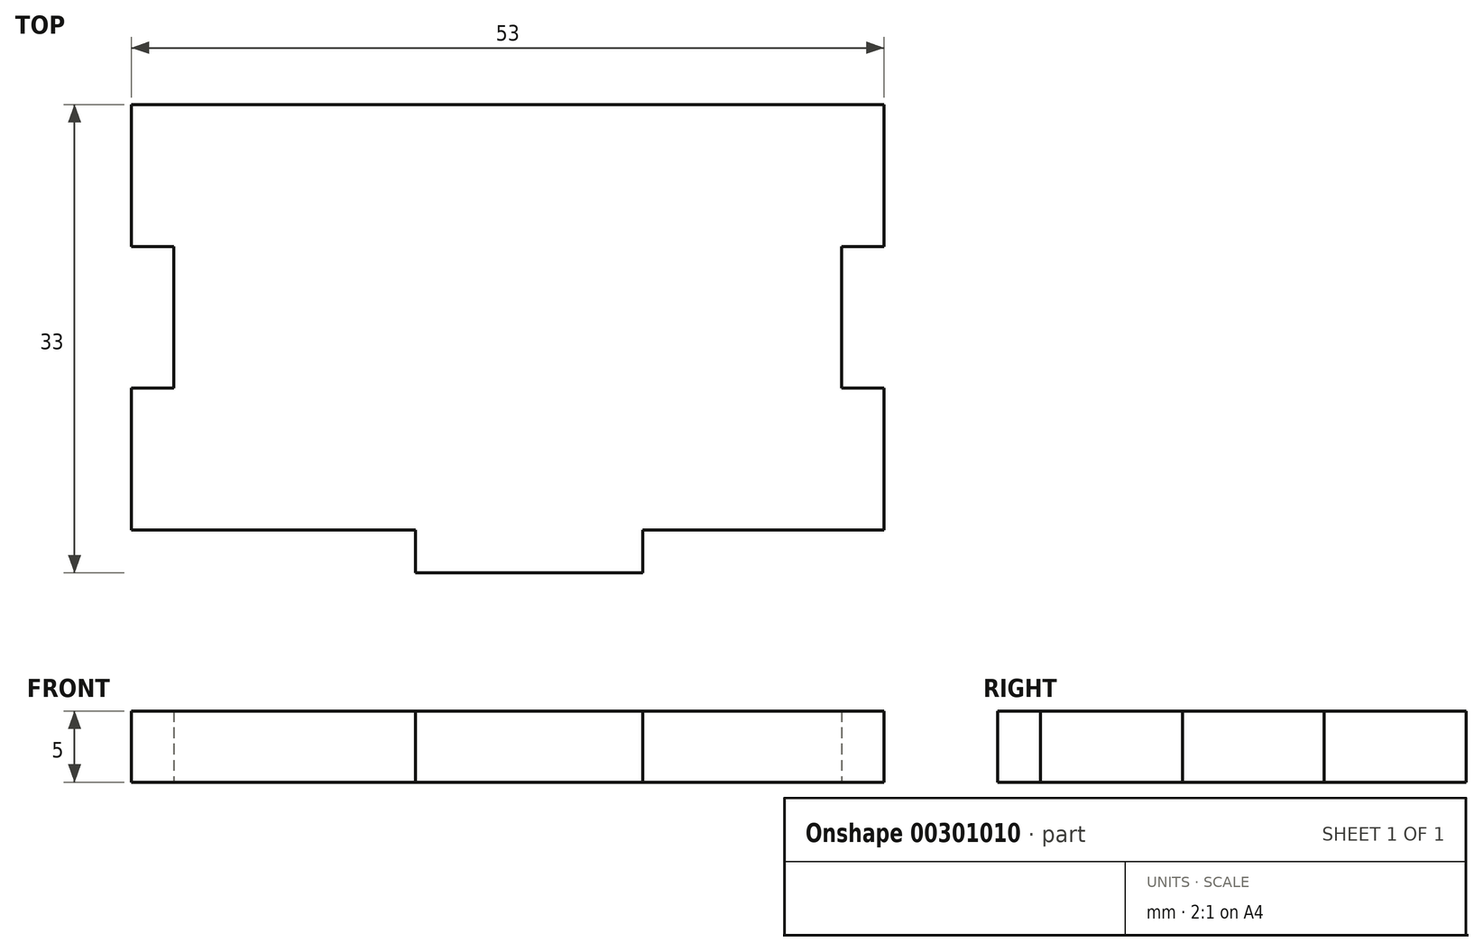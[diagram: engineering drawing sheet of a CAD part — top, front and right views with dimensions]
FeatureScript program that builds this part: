
annotation { "Feature Type Name" : "Feature", "Feature Type Description" : "" }
export const myFeature = defineFeature(function(context is Context, id is Id, definition is map)
    precondition{}
    {
        {
            var Q0;
            Q0=qCreatedBy(makeId("Top.planeOp"),FACE);
            var sketch = newSketch(context, id + "F0", { "sketchPlane" : qUnion([Q0])});
            skLineSegment(sketch, "E0.bottom", {"start": v(-26.5, 16.5) * mm, "end": v(26.5, 16.5) * mm});
            skLineSegment(sketch, "E1", {"start": v(-23.5, -13.5) * mm, "end": v(-6.5, -13.5) * mm});
            skLineSegment(sketch, "E2", {"start": v(26.5, -13.5) * mm, "end": v(9.5, -13.5) * mm});
            skLineSegment(sketch, "E3", {"start": v(-6.5, -13.5) * mm, "end": v(-6.5, -16.5) * mm});
            skLineSegment(sketch, "E4", {"start": v(-6.5, -16.5) * mm, "end": v(9.5, -16.5) * mm});
            skLineSegment(sketch, "E5", {"start": v(9.5, -16.5) * mm, "end": v(9.5, -13.5) * mm});
            skLineSegment(sketch, "E6", {"start": v(26.5, 16.5) * mm, "end": v(26.5, 6.5) * mm});
            skLineSegment(sketch, "E7", {"start": v(26.5, -13.5) * mm, "end": v(26.5, -3.5) * mm});
            skLineSegment(sketch, "E8", {"start": v(26.5, 6.5) * mm, "end": v(23.5, 6.5) * mm});
            skLineSegment(sketch, "E9", {"start": v(26.5, -3.5) * mm, "end": v(23.5, -3.5) * mm});
            skLineSegment(sketch, "E10", {"start": v(23.5, 6.5) * mm, "end": v(23.5, -3.5) * mm});
            skLineSegment(sketch, "E11.MirrorCS", {"start": v(-26.5, -3.5) * mm, "end": v(-23.5, -3.5) * mm});
            skLineSegment(sketch, "E12.MirrorCS", {"start": v(-26.5, 6.5) * mm, "end": v(-23.5, 6.5) * mm});
            skLineSegment(sketch, "E13.MirrorCS", {"start": v(-23.5, 6.5) * mm, "end": v(-23.5, -3.5) * mm});
            skLineSegment(sketch, "E14.MirrorCS", {"start": v(-26.5, -13.5) * mm, "end": v(-26.5, -3.5) * mm});
            skLineSegment(sketch, "E15.MirrorCS", {"start": v(-26.5, -13.5) * mm, "end": v(-9.5, -13.5) * mm});
            skLineSegment(sketch, "E16.MirrorCS", {"start": v(-26.5, 16.5) * mm, "end": v(-26.5, 6.5) * mm});
            skSolve(sketch);
        }
        {
            var Q0;
            Q0=makeQuery(id+"F0.imprint","IMPRINT",FACE,{"disambiguationData":[TD([[makeQuery(id+"F0.imprint","IMPRINT",EDGE,{"derivedFrom":sQuery(id+"F0.wireOp",EDGE,"E0.bottom")}),-1.0]])]});
            extrude(context, id + "F1", {"entities" : qUnion([Q0]), "depth" : 5 * mm, "offsetDistance" : 25 * mm});
        }
    });
